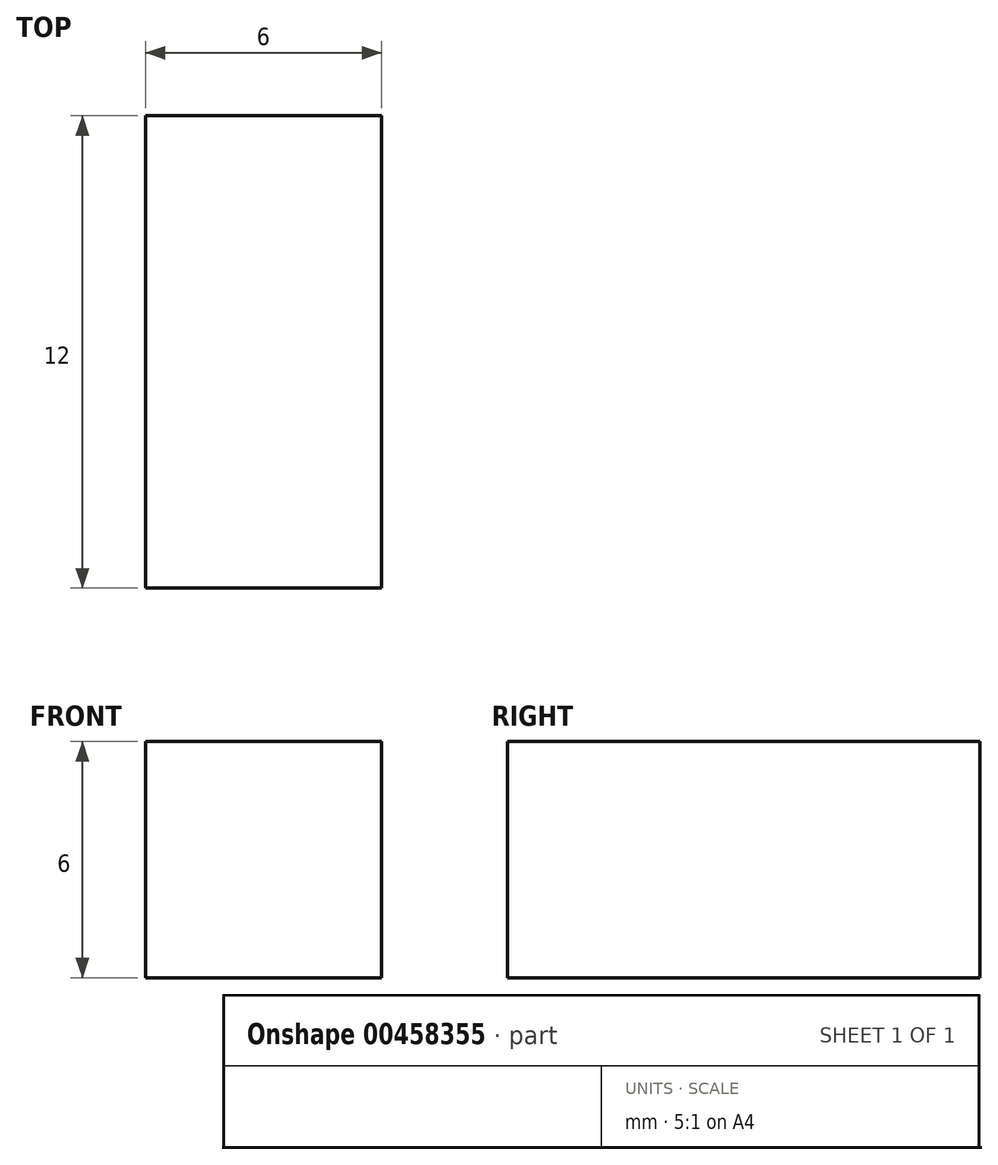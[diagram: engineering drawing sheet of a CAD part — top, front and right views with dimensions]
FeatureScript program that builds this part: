
annotation { "Feature Type Name" : "Feature", "Feature Type Description" : "" }
export const myFeature = defineFeature(function(context is Context, id is Id, definition is map)
    precondition{}
    {
        {
            var Q0;
            Q0=qCreatedBy(makeId("Front.planeOp"),FACE);
            var sketch = newSketch(context, id + "F0", { "sketchPlane" : qUnion([Q0])});
            skLineSegment(sketch, "E0.bottom", {"start": v(3, 6) * mm, "end": v(-3, 6) * mm});
            skLineSegment(sketch, "E0.top", {"start": v(3, 0) * mm, "end": v(-3, 0) * mm});
            skLineSegment(sketch, "E0.left", {"start": v(3, 6) * mm, "end": v(3, 0) * mm});
            skLineSegment(sketch, "E0.right", {"start": v(-3, 6) * mm, "end": v(-3, 0) * mm});
            skPoint(sketch, "E0.middle", {"position": v(0, 3) * mm});
            skSolve(sketch);
        }
        {
            var Q0;
            Q0=makeQuery(id+"F0.imprint","IMPRINT",FACE,{"disambiguationData":[TD([[makeQuery(id+"F0.imprint","IMPRINT",EDGE,{"derivedFrom":sQuery(id+"F0.wireOp",EDGE,"E0.bottom")}),1.0]])]});
            extrude(context, id + "F1", {"entities" : qUnion([Q0]), "depth" : 12 * mm});
        }
    });
